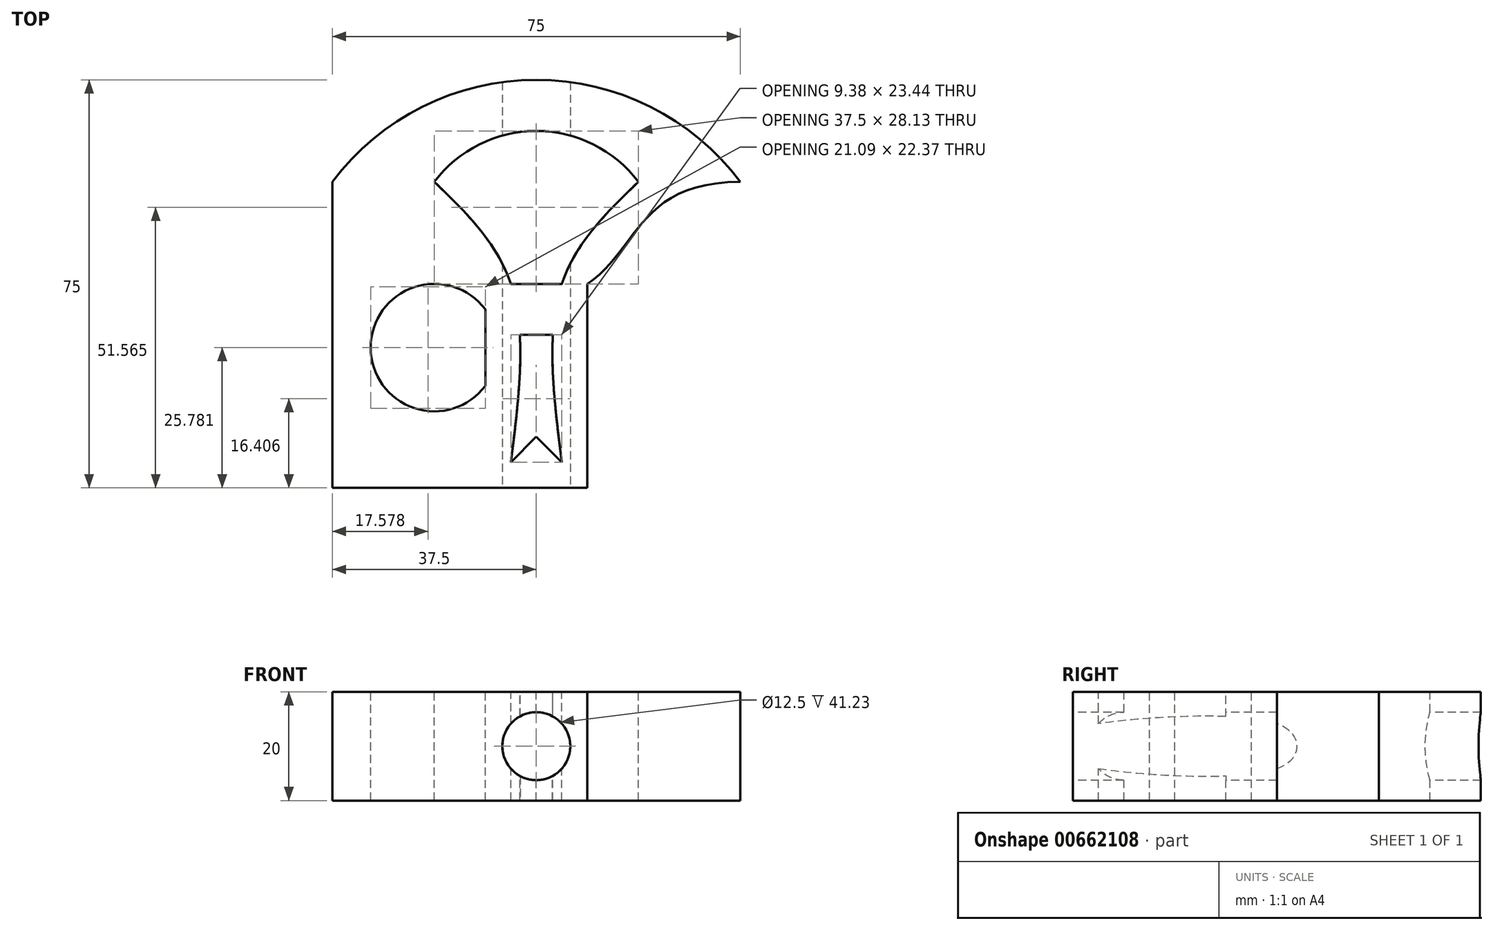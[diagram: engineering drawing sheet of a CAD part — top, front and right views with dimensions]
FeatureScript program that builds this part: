
annotation { "Feature Type Name" : "Feature", "Feature Type Description" : "" }
export const myFeature = defineFeature(function(context is Context, id is Id, definition is map)
    precondition{}
    {
        {
            var Q0;
            Q0=qCreatedBy(makeId("Top.planeOp"),FACE);
            var sketch = newSketch(context, id + "F0", { "sketchPlane" : qUnion([Q0])});
            skLineSegment(sketch, "E0.bottom", {"start": v(37.5, -37.5) * mm, "end": v(-37.5, -37.5) * mm});
            skLineSegment(sketch, "E0.top", {"start": v(37.5, 37.5) * mm, "end": v(-37.5, 37.5) * mm});
            skLineSegment(sketch, "E0.left", {"start": v(37.5, -37.5) * mm, "end": v(37.5, 37.5) * mm});
            skLineSegment(sketch, "E0.right", {"start": v(-37.5, -37.5) * mm, "end": v(-37.5, 37.5) * mm});
            skPoint(sketch, "E0.middle", {"position": v(0, 0) * mm});
            skSolve(sketch);
        }
        {
            var Q0;
            Q0=makeQuery(id+"F0.imprint","IMPRINT",FACE,{"disambiguationData":[TD([[makeQuery(id+"F0.imprint","IMPRINT",EDGE,{"derivedFrom":sQuery(id+"F0.wireOp",EDGE,"E0.bottom")}),-1.0]])]});
            extrude(context, id + "F1", {"entities" : qUnion([Q0]), "depth" : 10 * mm, "offsetDistance" : 25.4 * mm, "hasSecondDirection" : true, "secondDirectionOppositeDirection" : true, "secondDirectionDepth" : 10 * mm});
        }
        {
            var Q0;
            Q0=makeQuery(id+"F1.opExtrude","CAP_FACE",FACE,{"disambiguationData":[OSD([sQuery(id+"F0.wireOp",EDGE,"E0.bottom"),sQuery(id+"F0.wireOp",EDGE,"E0.top"),sQuery(id+"F0.wireOp",EDGE,"E0.left"),sQuery(id+"F0.wireOp",EDGE,"E0.right")])],"isStart":false});
            var sketch = newSketch(context, id + "F2", { "sketchPlane" : qUnion([Q0])});
            skPoint(sketch, "E1", {"position": v(-37.5, 0) * mm});
            skPoint(sketch, "E2", {"position": v(0, 37.5) * mm});
            skPoint(sketch, "E3", {"position": v(37.5, 0) * mm});
            skPoint(sketch, "E4", {"position": v(0, -37.5) * mm});
            skPoint(sketch, "E5", {"position": v(-37.5, -37.5) * mm});
            skPoint(sketch, "E6", {"position": v(-37.5, 37.5) * mm});
            skPoint(sketch, "E7", {"position": v(37.5, 37.5) * mm});
            skPoint(sketch, "E8", {"position": v(37.5, -37.5) * mm});
            skPoint(sketch, "E9", {"position": v(18.75, 0) * mm});
            skPoint(sketch, "E10", {"position": v(0, 18.75) * mm});
            skPoint(sketch, "E11", {"position": v(18.75, 18.75) * mm});
            skPoint(sketch, "E12", {"position": v(37.5, 18.75) * mm});
            skPoint(sketch, "E13", {"position": v(18.75, 37.5) * mm});
            skPoint(sketch, "E14.MirrorP", {"position": v(-18.75, 18.75) * mm});
            skPoint(sketch, "E15.MirrorP", {"position": v(-18.75, 0) * mm});
            skPoint(sketch, "E16.MirrorP", {"position": v(-37.5, 18.75) * mm});
            skPoint(sketch, "E17.MirrorP", {"position": v(-18.75, 37.5) * mm});
            skPoint(sketch, "E18.MirrorP", {"position": v(-18.75, -18.75) * mm});
            skPoint(sketch, "E19.MirrorP", {"position": v(18.75, -18.75) * mm});
            skPoint(sketch, "E20.MirrorP", {"position": v(0, -18.75) * mm});
            skPoint(sketch, "E21.MirrorP", {"position": v(-37.5, -18.75) * mm});
            skPoint(sketch, "E22.MirrorP", {"position": v(37.5, -18.75) * mm});
            skPoint(sketch, "E23.MirrorP", {"position": v(18.75, -37.5) * mm});
            skPoint(sketch, "E24.MirrorP", {"position": v(-18.75, -37.5) * mm});
            skArc(sketch, "E25", {"start": v(37.5, 18.75) * mm, "mid": v(0, 37.5) * mm, "end": v(-37.5, 18.75) * mm});
            skPoint(sketch, "E26", {"position": v(-9.38, -37.5) * mm});
            skPoint(sketch, "E27.MirrorP", {"position": v(9.38, -37.5) * mm});
            skPoint(sketch, "E28", {"position": v(-9.38, 0) * mm});
            skPoint(sketch, "E29", {"position": v(9.38, 0) * mm});
            skLineSegment(sketch, "E30", {"start": v(-9.38, 0) * mm, "end": v(-9.38, -37.5) * mm});
            skLineSegment(sketch, "E31", {"start": v(9.38, -37.5) * mm, "end": v(9.38, 0) * mm});
            skLineSegment(sketch, "E32", {"start": v(-9.38, -37.5) * mm, "end": v(9.38, -37.5) * mm});
            skArc(sketch, "E33", {"start": v(18.75, 18.75) * mm, "mid": v(0, 28.13) * mm, "end": v(-18.75, 18.75) * mm});
            skPoint(sketch, "E34", {"position": v(0, -28.12) * mm});
            skLineSegment(sketch, "E35", {"start": v(0, -28.12) * mm, "end": v(-9.37, -37.5) * mm});
            skLineSegment(sketch, "E36", {"start": v(0, -28.12) * mm, "end": v(9.37, -37.5) * mm});
            skPoint(sketch, "E37", {"position": v(4.69, -32.81) * mm});
            skPoint(sketch, "E37.positionSnap0", {"position": v(4.69, -32.81) * mm});
            skPoint(sketch, "E38", {"position": v(-4.69, -32.81) * mm});
            skPoint(sketch, "E38.positionSnap0", {"position": v(-4.69, -32.81) * mm});
            skPoint(sketch, "E39", {"position": v(4.69, 0) * mm});
            skPoint(sketch, "E40", {"position": v(-4.69, 0) * mm});
            skFitSpline(sketch, "E41", {"points": [v(-4.69, -32.81) * mm, v(-4.69, 0) * mm, v(-18.75, 18.75) * mm], "startDerivative": vector(8.32, 65.86) * mm, "endDerivative": vector(-37.73, 36.44) * mm});
            skPoint(sketch, "E42.MirrorP", {"position": v(12.99, 13.19) * mm});
            skPoint(sketch, "E43.MirrorP", {"position": v(3.18, -20.92) * mm});
            skFitSpline(sketch, "E44.MirrorCS", {"points": [v(4.69, -32.81) * mm, v(4.69, 0) * mm, v(18.75, 18.75) * mm], "startDerivative": vector(-8.32, 65.86) * mm, "endDerivative": vector(37.73, 36.44) * mm});
            skLineSegment(sketch, "E45", {"start": v(-4.69, 0) * mm, "end": v(4.69, 0) * mm});
            skLineSegment(sketch, "E46", {"start": v(-3.04, -9.38) * mm, "end": v(3.04, -9.38) * mm});
            skFitSpline(sketch, "E47", {"points": [v(-37.5, 18.75) * mm, v(-9.38, 0) * mm], "startDerivative": vector(56.25, 0) * mm, "endDerivative": vector(28.13, -18.75) * mm});
            skFitSpline(sketch, "E48", {"points": [v(9.38, 0) * mm, v(37.5, 18.75) * mm], "startDerivative": vector(28.13, 18.75) * mm, "endDerivative": vector(56.25, 0) * mm});
            skPoint(sketch, "E49", {"position": v(-28.12, -37.5) * mm});
            skPoint(sketch, "E50", {"position": v(-28.12, -18.75) * mm});
            skPoint(sketch, "E51", {"position": v(-28.12, 0) * mm});
            skPoint(sketch, "E52", {"position": v(28.13, -37.5) * mm});
            skPoint(sketch, "E53", {"position": v(28.13, -18.75) * mm});
            skPoint(sketch, "E54", {"position": v(28.13, 0) * mm});
            skLineSegment(sketch, "E55", {"start": v(-9.38, -37.5) * mm, "end": v(-18.75, -37.5) * mm});
            skLineSegment(sketch, "E56", {"start": v(9.38, -37.5) * mm, "end": v(18.75, -37.5) * mm});
            skFitSpline(sketch, "E57", {"points": [v(-28.12, -18.75) * mm, v(-18.75, -37.5) * mm], "startDerivative": vector(9.37, -18.75) * mm, "endDerivative": vector(9.37, -18.75) * mm});
            skFitSpline(sketch, "E58", {"points": [v(28.13, -18.75) * mm, v(18.75, -37.5) * mm], "startDerivative": vector(-9.37, -18.75) * mm, "endDerivative": vector(-9.38, -18.75) * mm});
            skPoint(sketch, "E59", {"position": v(-18.75, -11.72) * mm});
            skCircle(sketch, "E60", {"center": v(-18.75, -11.72) * mm, "radius": 11.72 * mm});
            skSolve(sketch);
        }
        {
            var Q0;
            {var subQ1=makeQuery(id+"F1.opExtrude","CAP_EDGE",EDGE,{"disambiguationData":[OSD([sQuery(id+"F0.wireOp",EDGE,"E0.right")])],"isStart":false});var subQ3=makeQuery(id+"F1.opExtrude","CAP_EDGE",EDGE,{"disambiguationData":[OSD([sQuery(id+"F0.wireOp",EDGE,"E0.top")])],"isStart":false});var subQ5=makeQuery(id+"F2.imprint","INTERSECT",VERTEX,{"derivedFrom":[subQ3,subQ1]});Q0=makeQuery(id+"F2.imprint","IMPRINT",FACE,{"disambiguationData":[TD([[makeQuery(id+"F2.imprint","IMPRINT",EDGE,{"disambiguationData":[TD([[subQ5,1.0]])],"derivedFrom":subQ3}),1.0]])]});}
            var Q1;
            {var subQ1=makeQuery(id+"F1.opExtrude","CAP_EDGE",EDGE,{"disambiguationData":[OSD([sQuery(id+"F0.wireOp",EDGE,"E0.left")])],"isStart":false});var subQ3=makeQuery(id+"F1.opExtrude","CAP_EDGE",EDGE,{"disambiguationData":[OSD([sQuery(id+"F0.wireOp",EDGE,"E0.top")])],"isStart":false});var subQ5=makeQuery(id+"F2.imprint","INTERSECT",VERTEX,{"derivedFrom":[subQ3,subQ1]});Q1=makeQuery(id+"F2.imprint","IMPRINT",FACE,{"disambiguationData":[TD([[makeQuery(id+"F2.imprint","IMPRINT",EDGE,{"disambiguationData":[TD([[subQ5,-1.0]])],"derivedFrom":subQ3}),1.0]])]});}
            var Q2;
            {var subQ0=sQuery(id+"F2.wireOp",EDGE,"098a3139-1fe5-439a-b696-199e2abdf080");Q2=makeQuery(id+"F2.imprint","IMPRINT",FACE,{"disambiguationData":[TD([[makeQuery(id+"F2.imprint","IMPRINT",EDGE,{"derivedFrom":subQ0}),1.0]])]});}
            var Q3;
            {var subQ0=sQuery(id+"F2.wireOp",EDGE,"526011ec-c277-4037-8a4e-62d01328d2f2");Q3=makeQuery(id+"F2.imprint","IMPRINT",FACE,{"disambiguationData":[TD([[makeQuery(id+"F2.imprint","IMPRINT",EDGE,{"derivedFrom":subQ0}),-1.0]])]});}
            var Q4;
            Q4=makeQuery(id+"F2.imprint","IMPRINT",FACE,{"disambiguationData":[TD([[makeQuery(id+"F2.imprint","IMPRINT",EDGE,{"derivedFrom":sQuery(id+"F2.wireOp",EDGE,"E33")}),1.0]])]});
            var Q5;
            {var subQ3=sQuery(id+"F2.wireOp",EDGE,"E46");Q5=makeQuery(id+"F2.imprint","IMPRINT",FACE,{"disambiguationData":[TD([[makeQuery(id+"F2.imprint","IMPRINT",EDGE,{"derivedFrom":subQ3}),-1.0]])]});}
            var Q6;
            {var subQ0=sQuery(id+"F2.wireOp",EDGE,"E30");Q6=makeQuery(id+"F2.imprint","IMPRINT",FACE,{"disambiguationData":[TD([[makeQuery(id+"F2.imprint","IMPRINT",EDGE,{"derivedFrom":subQ0}),-1.0]])]});}
            var Q7;
            {var subQ0=sQuery(id+"F2.wireOp",EDGE,"E31");Q7=makeQuery(id+"F2.imprint","IMPRINT",FACE,{"disambiguationData":[TD([[makeQuery(id+"F2.imprint","IMPRINT",EDGE,{"derivedFrom":subQ0}),-1.0]])]});}
            extrude(context, id + "F3", {"entities" : qUnion([Q0, Q1, Q2, Q3, Q4, Q5, Q6, Q7]), "operationType" : NewBodyOperationType.REMOVE, "oppositeDirection" : true, "depth" : 20 * mm, "offsetDistance" : 25.4 * mm});
        }
        {
            var Q0;
            Q0=makeQuery(id+"F1.opExtrude","SWEPT_FACE",FACE,{"disambiguationData":[OSD([sQuery(id+"F0.wireOp",EDGE,"E0.bottom")])]});
            var sketch = newSketch(context, id + "F4", { "sketchPlane" : qUnion([Q0])});
            skCircle(sketch, "E61", {"center": v(0, 0) * mm, "radius": 6.25 * mm});
            skSolve(sketch);
        }
        {
            var Q0;
            Q0=makeQuery(id+"F4.imprint","IMPRINT",FACE,{"disambiguationData":[TD([[makeQuery(id+"F4.imprint","IMPRINT",EDGE,{"derivedFrom":sQuery(id+"F4.wireOp",EDGE,"E61")}),1.0]])]});
            extrude(context, id + "F5", {"entities" : qUnion([Q0]), "operationType" : NewBodyOperationType.REMOVE, "oppositeDirection" : true, "depth" : 75 * mm, "offsetDistance" : 25.4 * mm});
        }
    });
